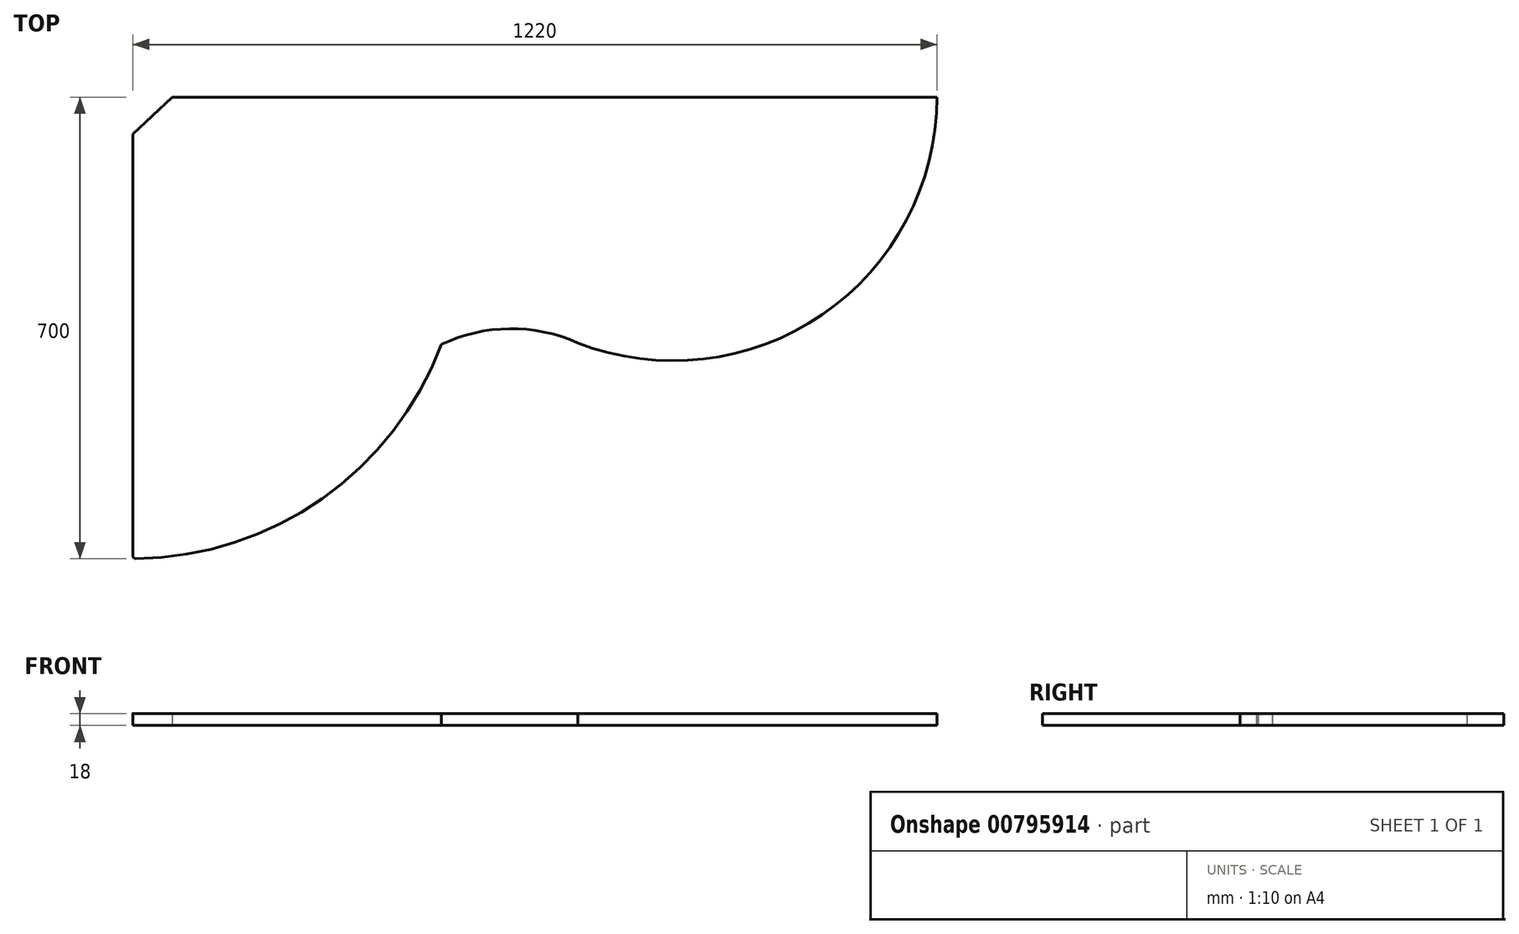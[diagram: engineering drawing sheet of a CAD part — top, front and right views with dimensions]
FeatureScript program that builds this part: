
annotation { "Feature Type Name" : "Feature", "Feature Type Description" : "" }
export const myFeature = defineFeature(function(context is Context, id is Id, definition is map)
    precondition{}
    {
        {
            var Q0;
            Q0=qCreatedBy(makeId("Top.planeOp"),FACE);
            var sketch = newSketch(context, id + "F0", { "sketchPlane" : qUnion([Q0])});
            skLineSegment(sketch, "E0.bottom", {"start": v(-616.15, 303.1) * mm, "end": v(603.85, 303.1) * mm});
            skLineSegment(sketch, "E0.top", {"start": v(-611.15, -396.9) * mm, "end": v(603.85, -396.9) * mm});
            skLineSegment(sketch, "E0.left", {"start": v(-616.15, 303.1) * mm, "end": v(-616.15, -391.9) * mm});
            skLineSegment(sketch, "E0.right", {"start": v(603.85, 303.1) * mm, "end": v(603.85, -396.9) * mm});
            skPoint(sketch, "E1", {"position": v(203.85, 303.1) * mm});
            skPoint(sketch, "E2", {"position": v(-616.15, 103.1) * mm});
            skPoint(sketch, "E3.visualSharp", {"position": v(-616.15, -396.9) * mm});
            skArc(sketch, "E3.filletArc", {"start": v(-616.15, -391.9) * mm, "mid": v(-614.68, -395.44) * mm, "end": v(-611.15, -396.9) * mm});
            skCircle(sketch, "E4", {"center": v(-616.15, 103.1) * mm, "radius": 500.02 * mm});
            skCircle(sketch, "E5", {"center": v(203.85, 303.1) * mm, "radius": 400 * mm});
            skPoint(sketch, "E6", {"position": v(-147.78, -72) * mm});
            skPoint(sketch, "E7", {"position": v(58.86, -69.7) * mm});
            skArc(sketch, "E8", {"start": v(58.86, -69.7) * mm, "mid": v(-44.7, -48.2) * mm, "end": v(-147.78, -72) * mm});
            skPoint(sketch, "E9", {"position": v(-616.15, 246.9) * mm});
            skPoint(sketch, "E10", {"position": v(-556.23, 303.1) * mm});
            skLineSegment(sketch, "E11", {"start": v(-616.15, 246.9) * mm, "end": v(-556.23, 303.1) * mm});
            skSolve(sketch);
        }
        {
            var Q0;
            {var subQ0=sQuery(id+"F0.wireOp",EDGE,"E3.filletArc");Q0=makeQuery(id+"F0.imprint","IMPRINT",FACE,{"disambiguationData":[TD([[makeQuery(id+"F0.imprint","IMPRINT",EDGE,{"derivedFrom":subQ0}),1.0]])]});}
            var Q1;
            {var subQ0=sQuery(id+"F0.wireOp",EDGE,"E5");var subQ1=sQuery(id+"F0.wireOp",EDGE,"E0.bottom");var subQ2=makeQuery(id+"F0.imprint","INTERSECT",VERTEX,{"derivedFrom":[subQ1,subQ0]});Q1=makeQuery(id+"F0.imprint","IMPRINT",FACE,{"disambiguationData":[TD([[makeQuery(id+"F0.imprint","IMPRINT",EDGE,{"disambiguationData":[TD([[subQ2,-1.0]])],"derivedFrom":subQ1}),-1.0]])]});}
            var Q2;
            {var subQ0=sQuery(id+"F0.wireOp",EDGE,"E8");var subQ1=sQuery(id+"F0.wireOp",EDGE,"E4");var subQ2=makeQuery(id+"F0.imprint","INTERSECT",VERTEX,{"derivedFrom":[subQ1,subQ0]});Q2=makeQuery(id+"F0.imprint","IMPRINT",FACE,{"disambiguationData":[TD([[makeQuery(id+"F0.imprint","IMPRINT",EDGE,{"disambiguationData":[TD([[subQ2,-1.0]])],"derivedFrom":subQ1}),-1.0]])]});}
            var Q3;
            {var subQ1=sQuery(id+"F0.wireOp",EDGE,"E0.bottom");var subQ5=sQuery(id+"F0.wireOp",EDGE,"E4");var subQ8=makeQuery(id+"F0.imprint","INTERSECT",VERTEX,{"derivedFrom":[subQ1,subQ5]});Q3=makeQuery(id+"F0.imprint","IMPRINT",FACE,{"disambiguationData":[TD([[makeQuery(id+"F0.imprint","IMPRINT",EDGE,{"disambiguationData":[TD([[subQ8,1.0]])],"derivedFrom":subQ5}),-1.0]])]});}
            extrude(context, id + "F1", {"entities" : qUnion([Q0, Q1, Q2, Q3]), "depth" : 18 * mm, "offsetDistance" : 25 * mm});
        }
    });
